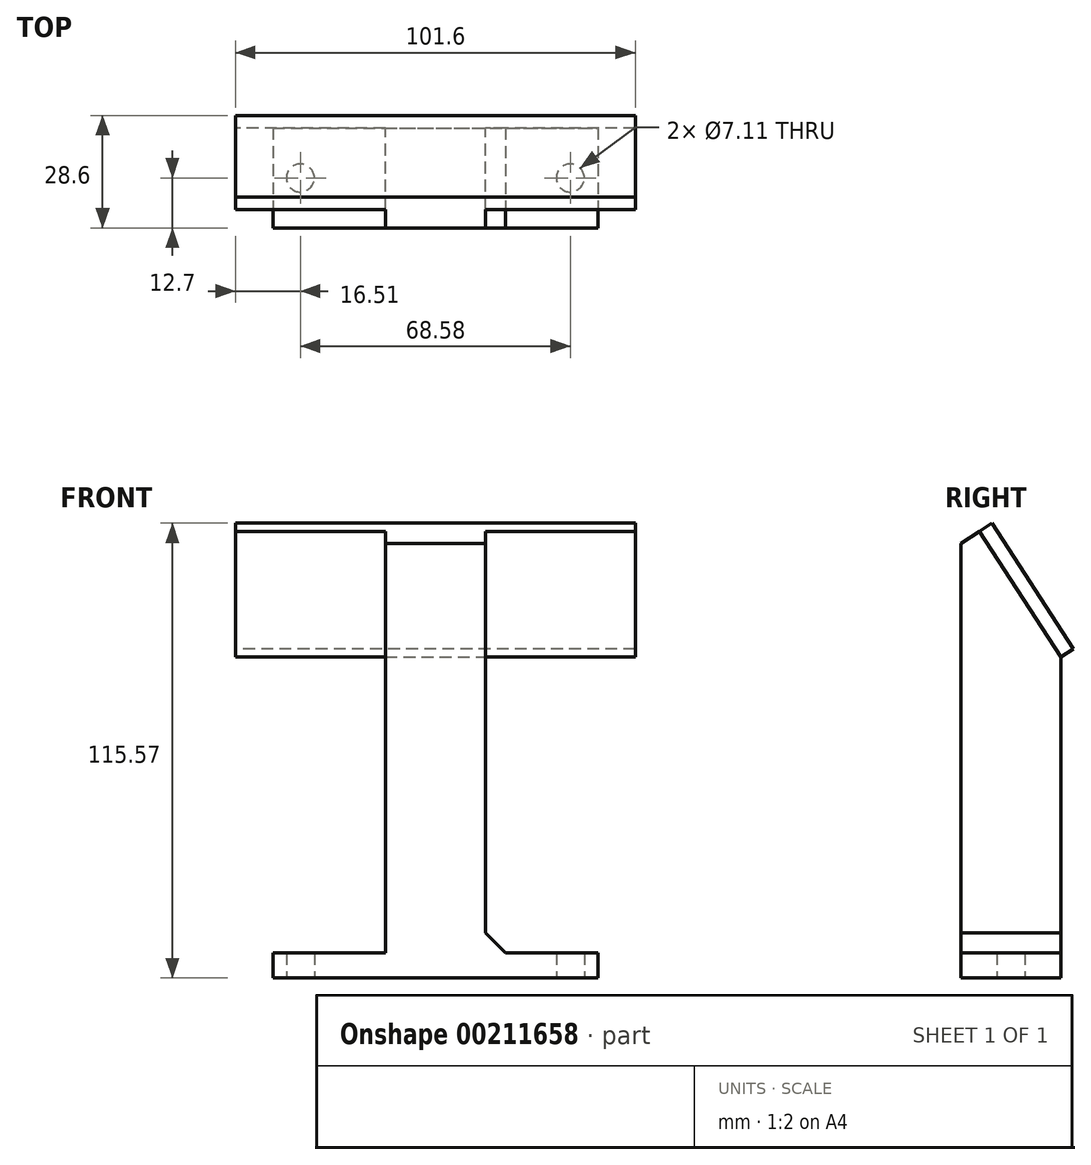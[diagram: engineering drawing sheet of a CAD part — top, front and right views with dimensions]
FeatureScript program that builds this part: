
annotation { "Feature Type Name" : "Feature", "Feature Type Description" : "" }
export const myFeature = defineFeature(function(context is Context, id is Id, definition is map)
    precondition{}
    {
        {
            var Q0;
            Q0=qCreatedBy(makeId("Top.planeOp"),FACE);
            var sketch = newSketch(context, id + "F0", { "sketchPlane" : qUnion([Q0])});
            skLineSegment(sketch, "E0.bottom", {"start": v(-41.28, 12.7) * mm, "end": v(41.28, 12.7) * mm});
            skLineSegment(sketch, "E0.top", {"start": v(-41.28, -12.7) * mm, "end": v(41.28, -12.7) * mm});
            skLineSegment(sketch, "E0.left", {"start": v(-41.27, 12.7) * mm, "end": v(-41.28, -12.7) * mm});
            skLineSegment(sketch, "E0.right", {"start": v(41.28, 12.7) * mm, "end": v(41.27, -12.7) * mm});
            skLineSegment(sketch, "E1", {"start": v(-34.3, 0) * mm, "end": v(34.3, 0) * mm, "construction": true});
            skLineSegment(sketch, "E2", {"start": v(0, 12.7) * mm, "end": v(0, -50.8) * mm, "construction": true});
            skCircle(sketch, "E3", {"center": v(-34.3, 0) * mm, "radius": 3.56 * mm});
            skCircle(sketch, "E4", {"center": v(34.3, 0) * mm, "radius": 3.56 * mm});
            skSolve(sketch);
        }
        {
            var Q0;
            Q0=makeQuery(id+"F0.imprint","IMPRINT",FACE,{"disambiguationData":[TD([[makeQuery(id+"F0.imprint","IMPRINT",EDGE,{"derivedFrom":sQuery(id+"F0.wireOp",EDGE,"E0.bottom")}),-1.0]])]});
            extrude(context, id + "F1", {"entities" : qUnion([Q0]), "depth" : 6.35 * mm});
        }
        {
            var Q0;
            Q0=makeQuery(id+"F1.opExtrude","CAP_FACE",FACE,{"disambiguationData":[OSD([sQuery(id+"F0.wireOp",EDGE,"E0.bottom"),sQuery(id+"F0.wireOp",EDGE,"E0.top"),sQuery(id+"F0.wireOp",EDGE,"E0.left"),sQuery(id+"F0.wireOp",EDGE,"E0.right"),sQuery(id+"F0.wireOp",EDGE,"E3"),sQuery(id+"F0.wireOp",EDGE,"E4")])],"isStart":false});
            var sketch = newSketch(context, id + "F2", { "sketchPlane" : qUnion([Q0])});
            skLineSegment(sketch, "E5.bottom", {"start": v(12.7, 12.7) * mm, "end": v(-12.7, 12.7) * mm});
            skLineSegment(sketch, "E5.top", {"start": v(12.7, -12.7) * mm, "end": v(-12.7, -12.7) * mm});
            skLineSegment(sketch, "E5.left", {"start": v(12.7, 12.7) * mm, "end": v(12.7, -12.7) * mm});
            skLineSegment(sketch, "E5.right", {"start": v(-12.7, 12.7) * mm, "end": v(-12.7, -12.7) * mm});
            skPoint(sketch, "E5.middle", {"position": v(0, 0) * mm});
            skSolve(sketch);
        }
        {
            var Q0;
            Q0=makeQuery(id+"F2.imprint","IMPRINT",FACE,{"disambiguationData":[TD([[makeQuery(id+"F2.imprint","IMPRINT",EDGE,{"derivedFrom":sQuery(id+"F2.wireOp",EDGE,"E5.bottom")}),-1.0]])]});
            extrude(context, id + "F3", {"entities" : qUnion([Q0]), "operationType" : NewBodyOperationType.ADD, "depth" : 114.3 * mm});
        }
        {
            var Q0;
            Q0=makeQuery(id+"F3.opExtrude","SWEPT_FACE",FACE,{"disambiguationData":[OSD([sQuery(id+"F2.wireOp",EDGE,"E5.left")])]});
            var sketch = newSketch(context, id + "F4", { "sketchPlane" : qUnion([Q0])});
            skLineSegment(sketch, "E6", {"start": v(-12.7, 120.65) * mm, "end": v(12.7, 81.54) * mm});
            skSolve(sketch);
        }
        {
            var Q0;
            {var subQ0=sQuery(id+"F4.wireOp",EDGE,"E6");Q0=makeQuery(id+"F4.imprint","IMPRINT",FACE,{"disambiguationData":[TD([[makeQuery(id+"F4.imprint","IMPRINT",EDGE,{"derivedFrom":subQ0}),1.0]])]});}
            extrude(context, id + "F5", {"entities" : qUnion([Q0]), "operationType" : NewBodyOperationType.REMOVE, "oppositeDirection" : true, "depth" : 25.4 * mm});
        }
        {
            var Q0;
            Q0=makeQuery(id+"F5.boolean.opBoolean","COPY",FACE,{"derivedFrom":makeQuery(id+"F5.opExtrude","SWEPT_FACE",FACE,{"disambiguationData":[OSD([sQuery(id+"F4.wireOp",EDGE,"E6")])]})});
            var sketch = newSketch(context, id + "F6", { "sketchPlane" : qUnion([Q0])});
            skLineSegment(sketch, "E7.bottom", {"start": v(-50.8, 61.47) * mm, "end": v(50.8, 61.47) * mm});
            skLineSegment(sketch, "E7.top", {"start": v(-50.8, 99.57) * mm, "end": v(50.8, 99.57) * mm});
            skLineSegment(sketch, "E7.left", {"start": v(-50.8, 61.47) * mm, "end": v(-50.8, 99.57) * mm});
            skLineSegment(sketch, "E7.right", {"start": v(50.8, 61.47) * mm, "end": v(50.8, 99.57) * mm});
            skPoint(sketch, "E7.middle", {"position": v(0, 80.52) * mm});
            skLineSegment(sketch, "E8", {"start": v(0, 99.57) * mm, "end": v(0, 61.47) * mm, "construction": true});
            skSolve(sketch);
        }
        {
            var Q0;
            {var subQ3=sQuery(id+"F6.wireOp",EDGE,"E7.right");Q0=makeQuery(id+"F6.imprint","IMPRINT",FACE,{"disambiguationData":[TD([[makeQuery(id+"F6.imprint","IMPRINT",EDGE,{"derivedFrom":subQ3}),1.0]])]});}
            var Q1;
            {var subQ0=sQuery(id+"F6.wireOp",EDGE,"E7.bottom");var subQ1=sQuery(id+"F4.wireOp",EDGE,"E6");var subQ2=makeQuery(id+"F5.boolean.opBoolean","COPY",EDGE,{"derivedFrom":makeQuery(id+"F5.opExtrude","CAP_EDGE",EDGE,{"disambiguationData":[OSD([subQ1])],"isStart":true})});var subQ3=makeQuery(id+"F6.imprint","INTERSECT",VERTEX,{"derivedFrom":[subQ2,subQ0]});var subQ4=makeQuery(id+"F5.boolean.opBoolean","COPY",EDGE,{"derivedFrom":makeQuery(id+"F5.opExtrude","CAP_EDGE",EDGE,{"disambiguationData":[OSD([subQ1])],"isStart":false})});var subQ5=makeQuery(id+"F6.imprint","INTERSECT",VERTEX,{"derivedFrom":[subQ4,subQ0]});Q1=makeQuery(id+"F6.imprint","IMPRINT",FACE,{"disambiguationData":[TD([[makeQuery(id+"F6.imprint","IMPRINT",EDGE,{"disambiguationData":[TD([[subQ3,1.0],[subQ5,-1.0]])],"derivedFrom":subQ0}),-1.0]])]});}
            var Q2;
            {var subQ3=sQuery(id+"F6.wireOp",EDGE,"E7.left");Q2=makeQuery(id+"F6.imprint","IMPRINT",FACE,{"disambiguationData":[TD([[makeQuery(id+"F6.imprint","IMPRINT",EDGE,{"derivedFrom":subQ3}),-1.0]])]});}
            extrude(context, id + "F7", {"entities" : qUnion([Q0, Q1, Q2]), "operationType" : NewBodyOperationType.ADD, "depth" : 3.8 * mm});
        }
        {
            var Q0;
            Q0=makeQuery(id+"F3.opExtrude","SWEPT_FACE",FACE,{"disambiguationData":[OSD([sQuery(id+"F2.wireOp",EDGE,"E5.left")])]});
            var sketch = newSketch(context, id + "F8", { "sketchPlane" : qUnion([Q0])});
            skLineSegment(sketch, "E9", {"start": v(-8.05, 113.5) * mm, "end": v(-12.7, 110.47) * mm});
            skSolve(sketch);
        }
        {
            var Q0;
            {var subQ0=sQuery(id+"F8.wireOp",EDGE,"E9");Q0=makeQuery(id+"F8.imprint","IMPRINT",FACE,{"disambiguationData":[TD([[makeQuery(id+"F8.imprint","IMPRINT",EDGE,{"derivedFrom":subQ0}),-1.0]])]});}
            extrude(context, id + "F9", {"entities" : qUnion([Q0]), "operationType" : NewBodyOperationType.REMOVE, "oppositeDirection" : true, "depth" : 25.4 * mm});
        }
        {
            var Q0;
            Q0=makeQuery(id+"F3.opExtrude","CAP_EDGE",EDGE,{"disambiguationData":[OSD([sQuery(id+"F2.wireOp",EDGE,"E5.left")])],"isStart":true});
            var Q1;
            Q1=makeQuery(id+"F3.opExtrude","CAP_EDGE",EDGE,{"disambiguationData":[OSD([sQuery(id+"F2.wireOp",EDGE,"E5.right")])],"isStart":true});
            var Q2;
            {var subQ0=sQuery(id+"F4.wireOp",EDGE,"E6");Q2=makeQuery(id+"F7.boolean.opBoolean","SPLIT",EDGE,{"disambiguationData":[TD([makeQuery(id+"F1.opExtrude","SWEPT_FACE",FACE,{"disambiguationData":[OSD([sQuery(id+"F0.wireOp",EDGE,"E0.bottom")])]})])],"derivedFrom":makeQuery(id+"F5.boolean.opBoolean","COPY",EDGE,{"derivedFrom":makeQuery(id+"F5.opExtrude","CAP_EDGE",EDGE,{"disambiguationData":[OSD([subQ0])],"isStart":true})})});}
            var Q3;
            {var subQ0=sQuery(id+"F4.wireOp",EDGE,"E6");Q3=makeQuery(id+"F7.boolean.opBoolean","SPLIT",EDGE,{"disambiguationData":[TD([makeQuery(id+"F1.opExtrude","SWEPT_FACE",FACE,{"disambiguationData":[OSD([sQuery(id+"F0.wireOp",EDGE,"E0.bottom")])]})])],"derivedFrom":makeQuery(id+"F5.boolean.opBoolean","COPY",EDGE,{"derivedFrom":makeQuery(id+"F5.opExtrude","CAP_EDGE",EDGE,{"disambiguationData":[OSD([subQ0])],"isStart":false})})});}
            chamfer(context, id + "F10", {"entities" : qUnion([Q0, Q1, Q2, Q3]), "width" : 5.08 * mm, "tangentPropagation" : true});
        }
    });
